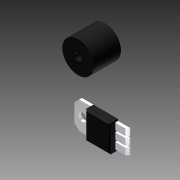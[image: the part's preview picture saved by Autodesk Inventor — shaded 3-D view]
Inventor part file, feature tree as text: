
AUTODESK INVENTOR PART (.ipt)
format: ipt  version: 2012 (Build 160160000, 160)  size: 256,000 bytes
history: native  units: in
note: dims shown in document units (in); Inventor stores cm internally (conversion verified against a paired STEP export)
features: extrude x6, chamfer x3, fillet x2, sketch x1
ambient origin geometry x8: Origin, YZ Plane, XZ Plane, XY Plane, X Axis, Y Axis, Z Axis, Center Point
bodies: Solid1 (feature_tree)
feature tree (12):
  sketch  "Sketch1"  dims[d0=3.2283in d1=2.1654in d2=0.689in d3=1.3976in d4=0.4528in d5=0.0984in d6=0.0394in d7=0.3937in d8=1.0825in d9=0.3543in d10=0.3937in d16=0.2362in d17=0.9in d18=0.7569in d19=0.1in d22=0.027in d24=0.3937in d25=0.1in d26=0.02in d27=0.177in d28=0.177in d29=0.1in d30=0.177in d31=0.02in d32=0.1181in d33=-0.0in d34=0.015in d35=0.125in d36=45.0deg d37=0.0394in d38=0.0in d39=0.07in d40=0.125in d41=45.0deg d42=0.1181in d43=0.0394in d44=0.0in d45=0.0394in d46=0.0in d47=0.035in d48=0.125in d49=45.0deg d50=0.005in d51=0.005in d52=0.1969in d53=0.0in d54=0.3937in d55=0.0in d56=0.0591in d57=0.2953in d58=0.0787in d59=0.0591in d60=0.0591in d61=0.0591in d62=0.0591in d63=0.0591in d64=0.0591in d65=0.0591in d66=0.1in d67=0.1in d68=0.1in d69=0.1in d70=0.1in d71=0.1in d72=0.1in d73=0.0591in d74=0.0591in d75=0.0591in d76=0.0591in d77=0.0591in d78=0.0591in d79=0.0591in d80=0.0591in d81=0.1in d82=0.1in d83=0.1in d84=0.1in d85=0.1in d86=0.1in d87=0.1in d88=0.0787in d89=0.2953in d90=0.0787in d91=0.0787in d92=0.0787in d93=0.0787in d94=0.0787in d95=0.0787in d96=0.0787in d97=0.1969in d98=0.1969in d99=0.1969in d100=0.1969in d101=0.0591in d102=0.0591in d104=0.1969in d105=0.1969in d106=0.0591in d107=0.0591in d108=0.0787in d109=0.0787in d111=0.1969in d112=0.1969in d113=0.1in d114=0.1in d115=0.1969in d116=0.1969in d117=0.1575in d118=0.1in d119=0.1969in d120=0.1969in d121=0.1969in d122=0.1969in d123=0.1969in d124=0.1969in d125=0.1969in d126=0.1969in d127=0.1181in d128=0.1181in d130=0.0394in d131=0.0394in d132=0.0394in d133=0.0394in]
  extrude  "Extrusion1"  Depth=2.1654in
  chamfer  "Chamfer1"  Distance=0.689in
  extrude  "Extrusion2"  Depth=1.3976in
  chamfer  "Chamfer2"  Distance=0.4528in
  extrude  "Extrusion3"  Depth=0.0984in
  extrude  "Extrusion4"  Depth=0.0394in
  chamfer  "Chamfer3"  Distance=0.3937in
  fillet  "Fillet1"  Radius=1.0825in
  fillet  "Fillet2"  Radius=0.3543in
  extrude  "Extrusion5"  Depth=0.3937in
  extrude  "Extrusion6"  Depth=0.2362in
